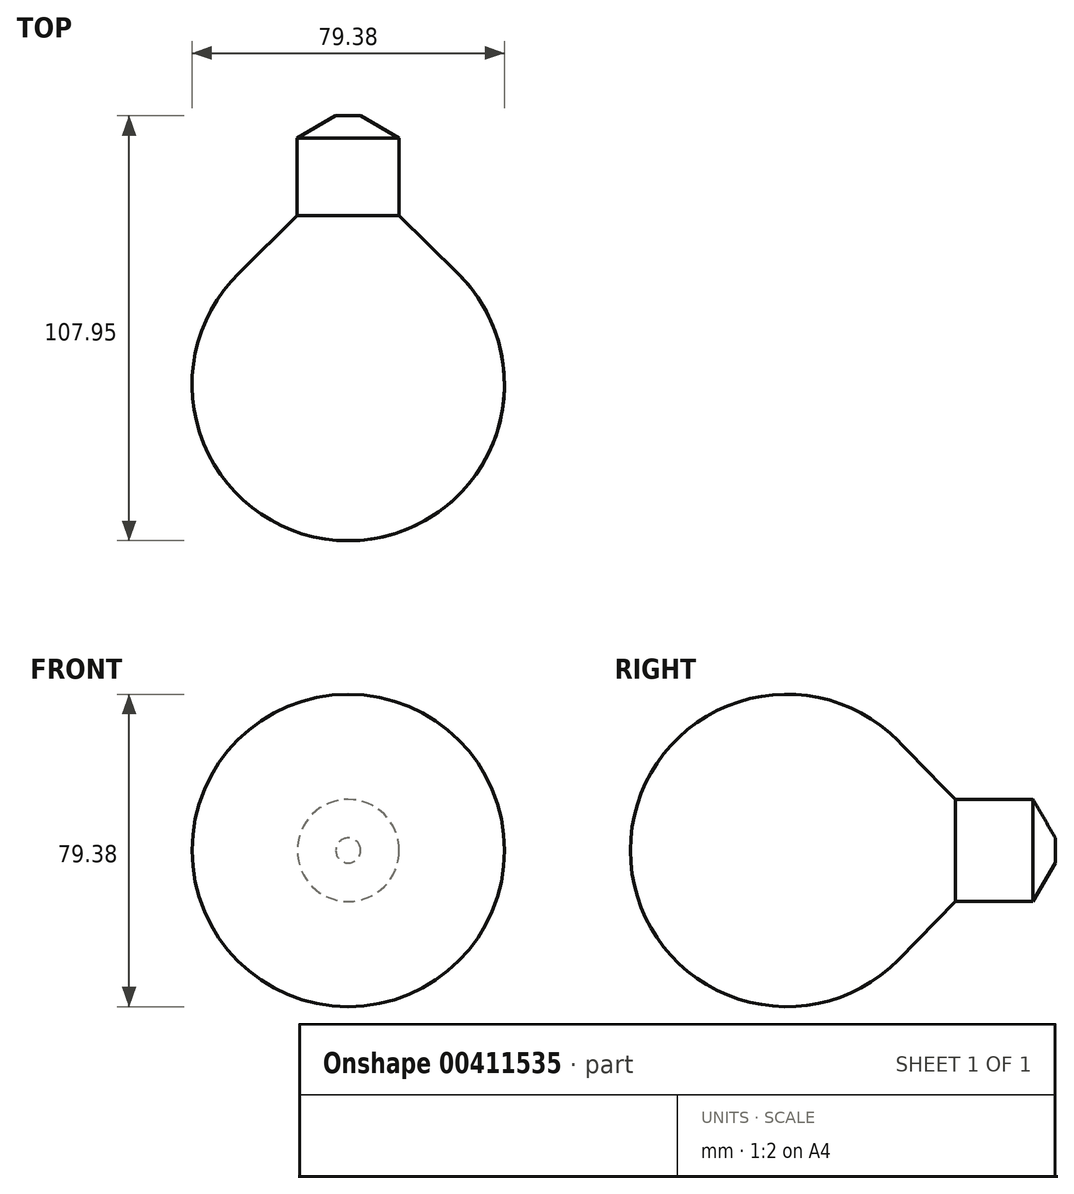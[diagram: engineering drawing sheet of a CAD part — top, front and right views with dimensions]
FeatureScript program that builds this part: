
annotation { "Feature Type Name" : "Feature", "Feature Type Description" : "" }
export const myFeature = defineFeature(function(context is Context, id is Id, definition is map)
    precondition{}
    {
        {
            var Q0;
            Q0=qCreatedBy(makeId("Top.planeOp"),FACE);
            var sketch = newSketch(context, id + "F0", { "sketchPlane" : qUnion([Q0])});
            skArc(sketch, "E0", {"start": v(0, -39.69) * mm, "mid": v(39.69, 0) * mm, "end": v(0, 39.69) * mm});
            skLineSegment(sketch, "E1", {"start": v(0, 39.69) * mm, "end": v(0, -39.69) * mm});
            skLineSegment(sketch, "E2", {"start": v(0, 39.69) * mm, "end": v(0, 68.26) * mm});
            skLineSegment(sketch, "E3", {"start": v(12.95, 62.62) * mm, "end": v(12.95, 42.86) * mm});
            skLineSegment(sketch, "E4", {"start": v(0, 68.26) * mm, "end": v(3.17, 68.26) * mm});
            skLineSegment(sketch, "E5", {"start": v(3.17, 68.26) * mm, "end": v(12.95, 62.62) * mm});
            skLineSegment(sketch, "E6", {"start": v(12.95, 42.86) * mm, "end": v(27.77, 28.36) * mm});
            skSolve(sketch);
        }
        {
            var Q0;
            Q0 = qSketchRegion(id + "F0", true);
            var Q1;
            Q1=sQuery(id+"F0.wireOp",EDGE,"E1");
            revolve(context, id + "F1", {"entities" : qUnion([Q0]), "axis" : qUnion([Q1]), "revolveType" : RevolveType.FULL});
        }
    });
